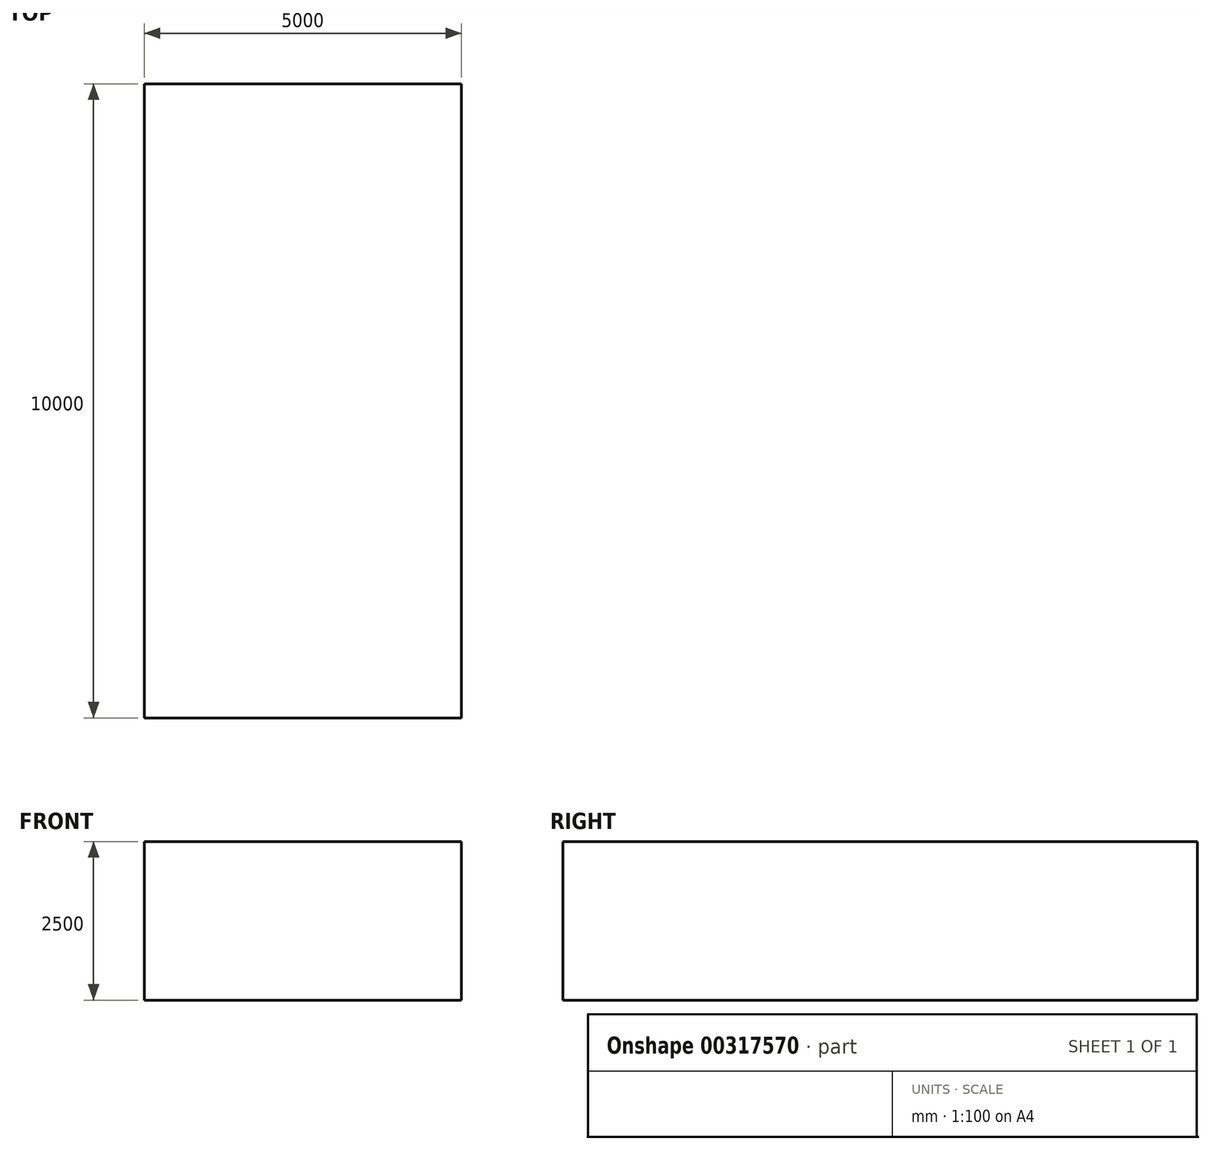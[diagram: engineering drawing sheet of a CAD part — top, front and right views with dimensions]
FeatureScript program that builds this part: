
annotation { "Feature Type Name" : "Feature", "Feature Type Description" : "" }
export const myFeature = defineFeature(function(context is Context, id is Id, definition is map)
    precondition{}
    {
        {
            var Q0;
            Q0=qCreatedBy(makeId("Front.planeOp"),FACE);
            var sketch = newSketch(context, id + "F0", { "sketchPlane" : qUnion([Q0])});
            skLineSegment(sketch, "E0.bottom", {"start": v(0, 0) * mm, "end": v(-5000, 0) * mm});
            skLineSegment(sketch, "E0.top", {"start": v(0, 2500) * mm, "end": v(-5000, 2500) * mm});
            skLineSegment(sketch, "E0.left", {"start": v(0, 0) * mm, "end": v(0, 2500) * mm});
            skLineSegment(sketch, "E0.right", {"start": v(-5000, 0) * mm, "end": v(-5000, 2500) * mm});
            skSolve(sketch);
        }
        {
            var Q0;
            Q0=makeQuery(id+"F0.imprint","IMPRINT",FACE,{"disambiguationData":[TD([[makeQuery(id+"F0.imprint","IMPRINT",EDGE,{"derivedFrom":sQuery(id+"F0.wireOp",EDGE,"E0.bottom")}),-1.0]])]});
            extrude(context, id + "F1", {"entities" : qUnion([Q0]), "depth" : 10000 * mm});
        }
    });
